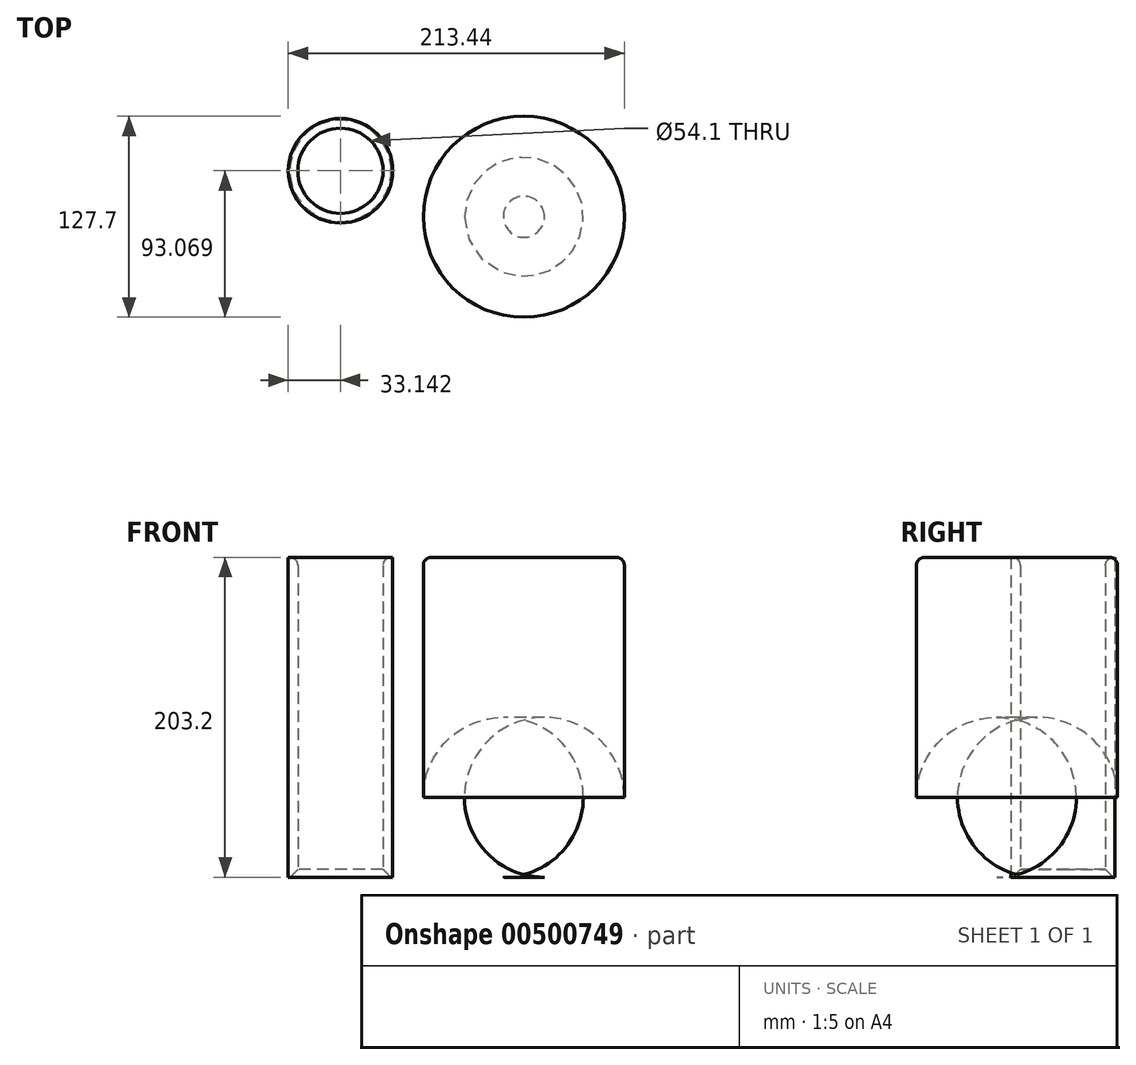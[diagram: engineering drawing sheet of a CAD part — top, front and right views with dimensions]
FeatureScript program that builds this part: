
annotation { "Feature Type Name" : "Feature", "Feature Type Description" : "" }
export const myFeature = defineFeature(function(context is Context, id is Id, definition is map)
    precondition{}
    {
        {
            var Q0;
            Q0=qCreatedBy(makeId("Top.planeOp"),FACE);
            var sketch = newSketch(context, id + "F0", { "sketchPlane" : qUnion([Q0])});
            skCircle(sketch, "E0", {"center": v(-116.45, 29.22) * mm, "radius": 16.08 * mm});
            skCircle(sketch, "E1", {"center": v(-116.45, 29.22) * mm, "radius": 21.05 * mm});
            skCircle(sketch, "E2", {"center": v(-116.45, 29.22) * mm, "radius": 27.05 * mm});
            skCircle(sketch, "E3", {"center": v(-116.45, 29.22) * mm, "radius": 33.15 * mm});
            skCircle(sketch, "E4", {"center": v(0, 0) * mm, "radius": 63.85 * mm});
            skSolve(sketch);
        }
        {
            var Q0;
            Q0 = qSketchRegion(id + "F0", true);
            extrude(context, id + "F1", {"entities" : qUnion([Q0]), "depth" : 203.2 * mm});
        }
        {
            var Q0;
            Q0=makeQuery(id+"F1.opExtrude","SWEPT_FACE",FACE,{"disambiguationData":[OSD([sQuery(id+"F0.wireOp",EDGE,"E3")])]});
            var Q1;
            Q1=makeQuery(id+"F1.opExtrude","CAP_EDGE",EDGE,{"disambiguationData":[OSD([sQuery(id+"F0.wireOp",EDGE,"E3")])],"isStart":true});
            var Q2;
            Q2=makeQuery(id+"F1.opExtrude","CAP_EDGE",EDGE,{"disambiguationData":[OSD([sQuery(id+"F0.wireOp",EDGE,"E4")])],"isStart":true});
            fillet(context, id + "F2", {"entities" : qUnion([Q0, Q1, Q2]), "radius" : 50.8 * mm, "tangentPropagation" : true, "allowEdgeOverflow" : false});
        }
        {
            var Q0;
            Q0=makeQuery(id+"F1.opExtrude","CAP_EDGE",EDGE,{"disambiguationData":[OSD([sQuery(id+"F0.wireOp",EDGE,"E4")])],"isStart":false});
            var Q1;
            Q1=makeQuery(id+"F1.opExtrude","CAP_EDGE",EDGE,{"disambiguationData":[OSD([sQuery(id+"F0.wireOp",EDGE,"E2")])],"isStart":false});
            fillet(context, id + "F3", {"entities" : qUnion([Q0, Q1]), "radius" : 5.08 * mm, "tangentPropagation" : true, "allowEdgeOverflow" : false});
        }
        {
            var Q0;
            Q0=makeQuery(id+"F1.opExtrude","SWEPT_FACE",FACE,{"disambiguationData":[OSD([sQuery(id+"F0.wireOp",EDGE,"E2")])]});
            var Q1;
            Q1=makeQuery(id+"F1.opExtrude","SWEPT_FACE",FACE,{"disambiguationData":[OSD([sQuery(id+"F0.wireOp",EDGE,"E4")])]});
            chamfer(context, id + "F4", {"entities" : qUnion([Q0, Q1]), "width" : 5.08 * mm, "tangentPropagation" : true});
        }
    });
